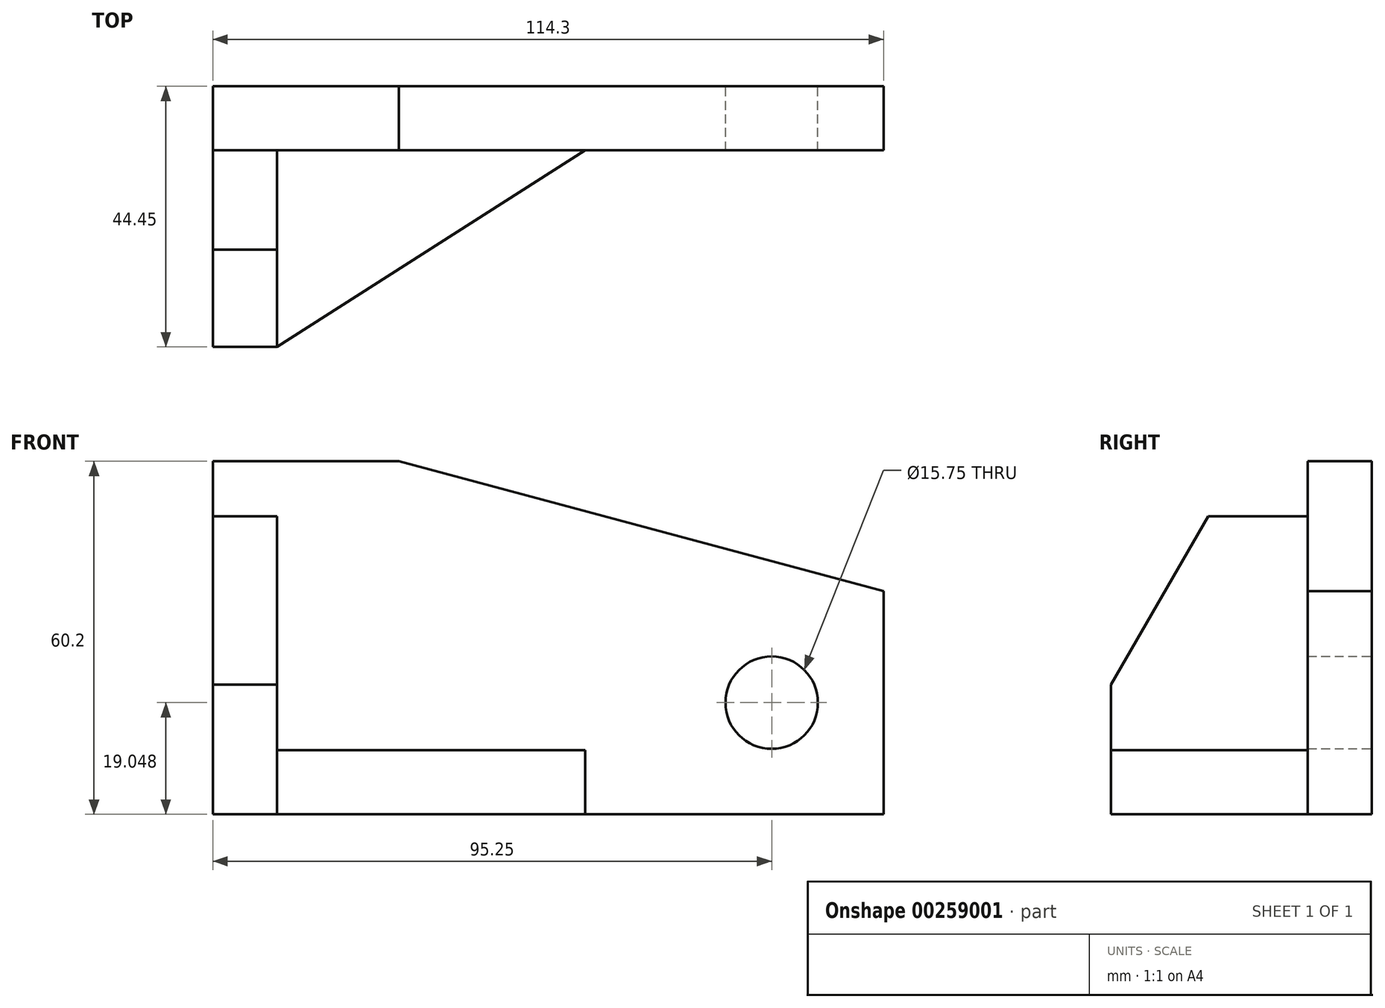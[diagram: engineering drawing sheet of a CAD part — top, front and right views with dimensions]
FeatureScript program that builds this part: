
annotation { "Feature Type Name" : "Feature", "Feature Type Description" : "" }
export const myFeature = defineFeature(function(context is Context, id is Id, definition is map)
    precondition{}
    {
        {
            var Q0;
            Q0=qCreatedBy(makeId("Front.planeOp"),FACE);
            var sketch = newSketch(context, id + "F0", { "sketchPlane" : qUnion([Q0])});
            skLineSegment(sketch, "E0.bottom", {"start": v(-51.55, 28.48) * mm, "end": v(62.75, 28.48) * mm});
            skLineSegment(sketch, "E0.top", {"start": v(-51.55, -31.72) * mm, "end": v(62.75, -31.72) * mm});
            skLineSegment(sketch, "E0.left", {"start": v(-51.55, 28.48) * mm, "end": v(-51.55, -31.72) * mm});
            skLineSegment(sketch, "E0.right", {"start": v(62.75, 28.48) * mm, "end": v(62.75, -31.72) * mm});
            skLineSegment(sketch, "E1.top", {"start": v(-51.55, 19.08) * mm, "end": v(-40.63, 19.08) * mm});
            skLineSegment(sketch, "E1.right", {"start": v(-40.63, -31.72) * mm, "end": v(-40.63, 19.08) * mm});
            skLineSegment(sketch, "E2.top", {"start": v(-40.63, -20.8) * mm, "end": v(11.95, -20.8) * mm});
            skLineSegment(sketch, "E2.right", {"start": v(11.95, -31.72) * mm, "end": v(11.95, -20.8) * mm});
            skLineSegment(sketch, "E3", {"start": v(62.75, -12.67) * mm, "end": v(43.7, -12.67) * mm, "construction": true});
            skLineSegment(sketch, "E4", {"start": v(43.7, -12.67) * mm, "end": v(43.7, -31.72) * mm, "construction": true});
            skCircle(sketch, "E5", {"center": v(43.7, -12.67) * mm, "radius": 7.87 * mm});
            skSolve(sketch);
        }
        {
            var Q0;
            {var subQ6=sQuery(id+"F0.wireOp",EDGE,"E1.top");Q0=makeQuery(id+"F0.imprint","IMPRINT",FACE,{"disambiguationData":[TD([[makeQuery(id+"F0.imprint","IMPRINT",EDGE,{"derivedFrom":subQ6}),-1.0]])]});}
            var Q1;
            {var subQ4=sQuery(id+"F0.wireOp",EDGE,"E2.top");Q1=makeQuery(id+"F0.imprint","IMPRINT",FACE,{"disambiguationData":[TD([[makeQuery(id+"F0.imprint","IMPRINT",EDGE,{"derivedFrom":subQ4}),-1.0]])]});}
            extrude(context, id + "F1", {"entities" : qUnion([Q0, Q1]), "depth" : 44.45 * mm});
        }
        {
            var Q0;
            {var subQ2=sQuery(id+"F0.wireOp",EDGE,"E0.bottom");Q0=makeQuery(id+"F0.imprint","IMPRINT",FACE,{"disambiguationData":[TD([[makeQuery(id+"F0.imprint","IMPRINT",EDGE,{"derivedFrom":subQ2}),-1.0]])]});}
            extrude(context, id + "F2", {"entities" : qUnion([Q0]), "operationType" : NewBodyOperationType.ADD, "depth" : 10.92 * mm});
        }
        {
            var Q0;
            Q0=makeQuery(id+"F1.opExtrude","CAP_EDGE",EDGE,{"disambiguationData":[OSD([sQuery(id+"F0.wireOp",EDGE,"E2.right")])],"isStart":false});
            chamfer(context, id + "F3", {"entities" : qUnion([Q0]), "chamferType" : ChamferType.TWO_OFFSETS, "width1" : 52.58 * mm, "oppositeDirection" : false, "width2" : 33.53 * mm, "tangentPropagation" : true});
        }
        {
            var Q0;
            Q0=makeQuery(id+"F2.opExtrude","SWEPT_EDGE",EDGE,{"disambiguationData":[OSD([sQuery(id+"F0.wireOp",EDGE,"E0.bottom"),sQuery(id+"F0.wireOp",EDGE,"E0.right")])]});
            chamfer(context, id + "F4", {"entities" : qUnion([Q0]), "chamferType" : ChamferType.OFFSET_ANGLE, "width" : 82.55 * mm, "oppositeDirection" : false, "angle" : 15 * degree, "tangentPropagation" : true});
        }
        {
            var Q0;
            Q0=makeQuery(id+"F1.opExtrude","CAP_EDGE",EDGE,{"disambiguationData":[OSD([sQuery(id+"F0.wireOp",EDGE,"E1.top")])],"isStart":false});
            chamfer(context, id + "F5", {"entities" : qUnion([Q0]), "chamferType" : ChamferType.OFFSET_ANGLE, "width" : 16.56 * mm, "oppositeDirection" : false, "angle" : 60 * degree, "tangentPropagation" : true});
        }
    });
